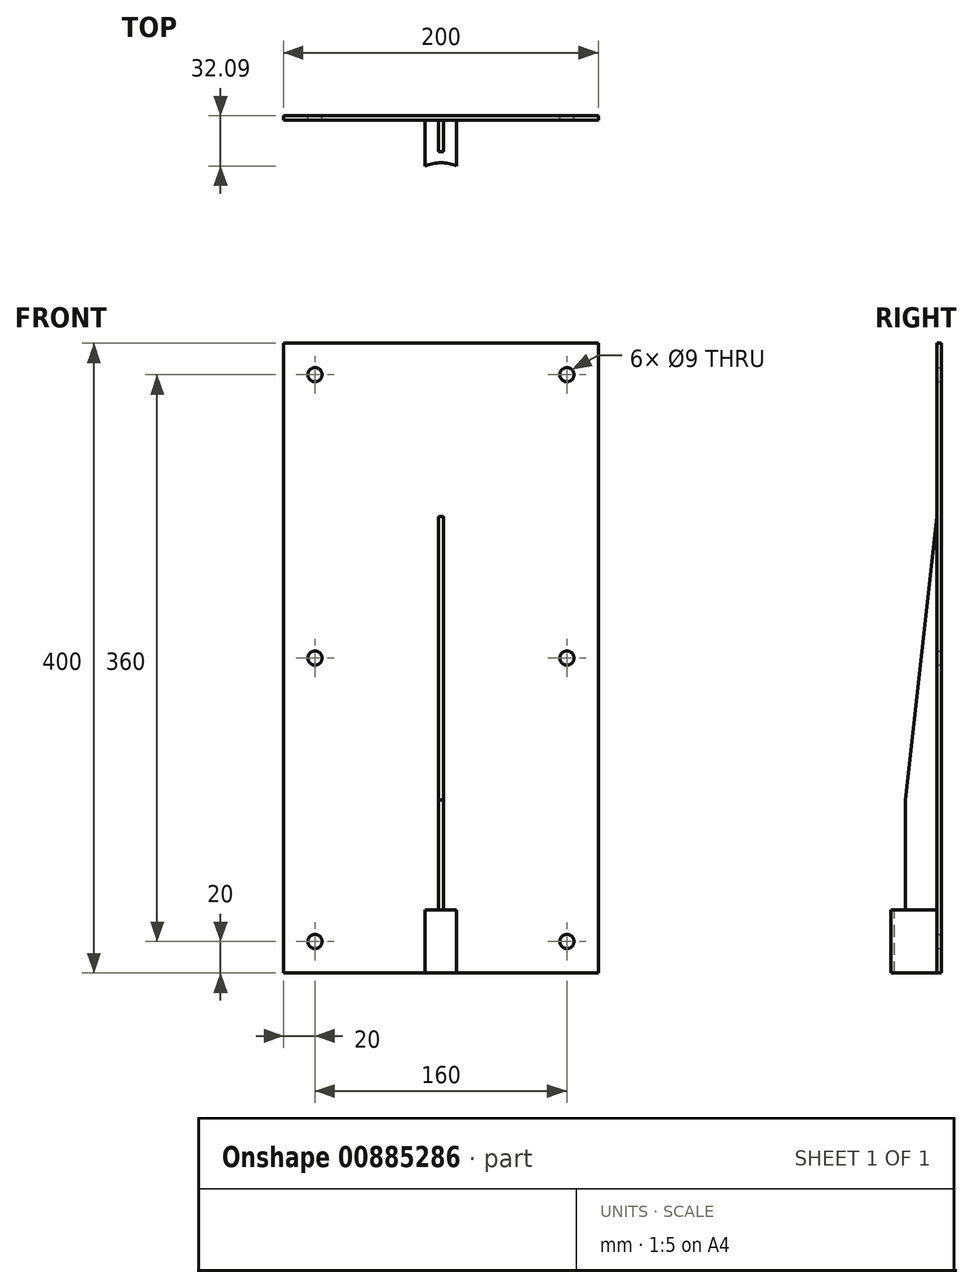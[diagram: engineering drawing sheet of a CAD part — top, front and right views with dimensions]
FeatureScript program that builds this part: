
annotation { "Feature Type Name" : "Feature", "Feature Type Description" : "" }
export const myFeature = defineFeature(function(context is Context, id is Id, definition is map)
    precondition{}
    {
        {
            var Q0;
            Q0=qCreatedBy(makeId("Front.planeOp"),FACE);
            var sketch = newSketch(context, id + "F0", { "sketchPlane" : qUnion([Q0])});
            skLineSegment(sketch, "E0.bottom", {"start": v(100, 200) * mm, "end": v(-100, 200) * mm});
            skLineSegment(sketch, "E0.top", {"start": v(100, -200) * mm, "end": v(-100, -200) * mm});
            skLineSegment(sketch, "E0.left", {"start": v(100, 200) * mm, "end": v(100, -200) * mm});
            skLineSegment(sketch, "E0.right", {"start": v(-100, 200) * mm, "end": v(-100, -200) * mm});
            skPoint(sketch, "E0.middle", {"position": v(0, 0) * mm});
            skCircle(sketch, "E1", {"center": v(-80, 180) * mm, "radius": 4.5 * mm});
            skCircle(sketch, "E2", {"center": v(-80, 0) * mm, "radius": 4.5 * mm});
            skCircle(sketch, "E3", {"center": v(-80, -180) * mm, "radius": 4.5 * mm});
            skCircle(sketch, "E4", {"center": v(80, -180) * mm, "radius": 4.5 * mm});
            skCircle(sketch, "E5", {"center": v(80, 0) * mm, "radius": 4.5 * mm});
            skCircle(sketch, "E6", {"center": v(80, 180) * mm, "radius": 4.5 * mm});
            skSolve(sketch);
        }
        {
            var Q0;
            Q0=makeQuery(id+"F0.imprint","IMPRINT",FACE,{"disambiguationData":[TD([[makeQuery(id+"F0.imprint","IMPRINT",EDGE,{"derivedFrom":sQuery(id+"F0.wireOp",EDGE,"E0.bottom")}),1.0]])]});
            extrude(context, id + "F1", {"entities" : qUnion([Q0]), "depth" : 3 * mm, "offsetDistance" : 25 * mm});
        }
        {
            var Q0;
            Q0=makeQuery(id+"F1.opExtrude","CAP_FACE",FACE,{"disambiguationData":[OSD([sQuery(id+"F0.wireOp",EDGE,"E0.bottom"),sQuery(id+"F0.wireOp",EDGE,"E0.top"),sQuery(id+"F0.wireOp",EDGE,"E0.left"),sQuery(id+"F0.wireOp",EDGE,"E0.right"),sQuery(id+"F0.wireOp",EDGE,"E1"),sQuery(id+"F0.wireOp",EDGE,"E2"),sQuery(id+"F0.wireOp",EDGE,"E3"),sQuery(id+"F0.wireOp",EDGE,"E4"),sQuery(id+"F0.wireOp",EDGE,"E5"),sQuery(id+"F0.wireOp",EDGE,"E6")])],"isStart":false});
            var sketch = newSketch(context, id + "F2", { "sketchPlane" : qUnion([Q0])});
            skPoint(sketch, "E7", {"position": v(0, -200) * mm});
            skLineSegment(sketch, "E8", {"start": v(-10, -200) * mm, "end": v(-10, -160) * mm});
            skLineSegment(sketch, "E9", {"start": v(-10, -160) * mm, "end": v(10, -160) * mm});
            skLineSegment(sketch, "E10", {"start": v(10, -160) * mm, "end": v(10, -200) * mm});
            skLineSegment(sketch, "E11", {"start": v(0, -160) * mm, "end": v(0, -215.78) * mm, "construction": true});
            skSolve(sketch);
        }
        {
            var Q0;
            {var subQ0=sQuery(id+"F2.wireOp",EDGE,"E8");Q0=makeQuery(id+"F2.imprint","IMPRINT",FACE,{"disambiguationData":[TD([[makeQuery(id+"F2.imprint","IMPRINT",EDGE,{"derivedFrom":subQ0}),-1.0]])]});}
            extrude(context, id + "F3", {"entities" : qUnion([Q0]), "depth" : 30 * mm, "offsetDistance" : 25 * mm});
        }
        {
            var Q0;
            Q0=makeQuery(id+"F3.opExtrude","SWEPT_FACE",FACE,{"disambiguationData":[OSD([sQuery(id+"F2.wireOp",EDGE,"E9")])]});
            var sketch = newSketch(context, id + "F4", { "sketchPlane" : qUnion([Q0])});
            skLineSegment(sketch, "E12", {"start": v(0, -33) * mm, "end": v(0, -19.28) * mm, "construction": true});
            skLineSegment(sketch, "E13", {"start": v(0, -33) * mm, "end": v(0, -55) * mm, "construction": true});
            skCircle(sketch, "E14", {"center": v(0, -55) * mm, "radius": 25 * mm});
            skLineSegment(sketch, "E15", {"start": v(0, -19.28) * mm, "end": v(0, -3) * mm, "construction": true});
            skLineSegment(sketch, "E16", {"start": v(-10, -23) * mm, "end": v(10, -23) * mm, "construction": true});
            skLineSegment(sketch, "E17", {"start": v(-1.5, -23) * mm, "end": v(-1.5, -3) * mm});
            skLineSegment(sketch, "E18", {"start": v(1.5, -23) * mm, "end": v(1.5, -3) * mm});
            skLineSegment(sketch, "E19", {"start": v(-1.5, -23) * mm, "end": v(1.5, -23) * mm});
            skSolve(sketch);
        }
        {
            var Q0;
            {var subQ1=sQuery(id+"F2.wireOp",EDGE,"E9");var subQ6=makeQuery(id+"F3.opExtrude","CAP_EDGE",EDGE,{"disambiguationData":[OSD([subQ1])],"isStart":false});Q0=makeQuery(id+"F4.imprint","IMPRINT",FACE,{"disambiguationData":[TD([[makeQuery(id+"F4.imprint","IMPRINT",EDGE,{"derivedFrom":subQ6}),1.0]])]});}
            extrude(context, id + "F5", {"entities" : qUnion([Q0]), "operationType" : NewBodyOperationType.REMOVE, "oppositeDirection" : true, "depth" : 42.5 * mm, "offsetDistance" : 25 * mm});
        }
        {
            var Q0;
            {var subQ0=sQuery(id+"F4.wireOp",EDGE,"E17");Q0=makeQuery(id+"F4.imprint","IMPRINT",FACE,{"disambiguationData":[TD([[makeQuery(id+"F4.imprint","IMPRINT",EDGE,{"derivedFrom":subQ0}),-1.0]])]});}
            extrude(context, id + "F6", {"entities" : qUnion([Q0]), "depth" : 250 * mm, "offsetDistance" : 25 * mm});
        }
        {
            var Q0;
            Q0=makeQuery(id+"F6.opExtrude","SWEPT_FACE",FACE,{"disambiguationData":[OSD([sQuery(id+"F4.wireOp",EDGE,"E18")])]});
            var sketch = newSketch(context, id + "F7", { "sketchPlane" : qUnion([Q0])});
            skLineSegment(sketch, "E20", {"start": v(-23, -90) * mm, "end": v(-3, -90) * mm, "construction": true});
            skLineSegment(sketch, "E21", {"start": v(-3, 90) * mm, "end": v(-23, -90) * mm});
            skSolve(sketch);
        }
        {
            var Q0;
            {var subQ0=sQuery(id+"F7.wireOp",EDGE,"E21");Q0=makeQuery(id+"F7.imprint","IMPRINT",FACE,{"disambiguationData":[TD([[makeQuery(id+"F7.imprint","IMPRINT",EDGE,{"derivedFrom":subQ0}),-1.0]])]});}
            extrude(context, id + "F8", {"entities" : qUnion([Q0]), "operationType" : NewBodyOperationType.REMOVE, "oppositeDirection" : true, "depth" : 25 * mm, "offsetDistance" : 25 * mm});
        }
    });
